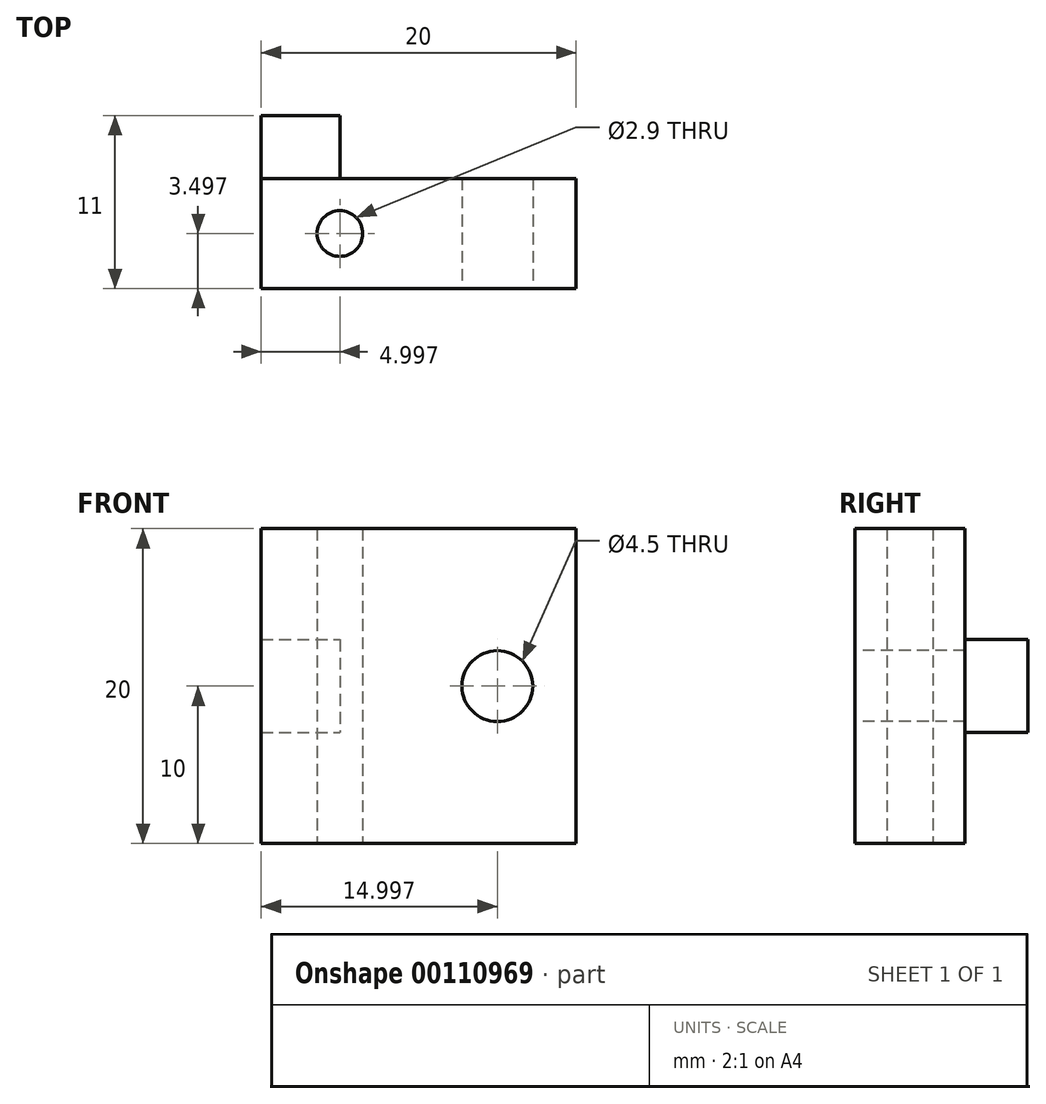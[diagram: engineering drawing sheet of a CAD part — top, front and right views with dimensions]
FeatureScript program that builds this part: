
annotation { "Feature Type Name" : "Feature", "Feature Type Description" : "" }
export const myFeature = defineFeature(function(context is Context, id is Id, definition is map)
    precondition{}
    {
        {
            var Q0;
            Q0=qCreatedBy(makeId("Top.planeOp"),FACE);
            var sketch = newSketch(context, id + "F0", { "sketchPlane" : qUnion([Q0])});
            skLineSegment(sketch, "E0.bottom", {"start": v(-14.26, 17.83) * mm, "end": v(5.74, 17.83) * mm});
            skLineSegment(sketch, "E0.top", {"start": v(-14.26, 24.83) * mm, "end": v(5.74, 24.83) * mm});
            skLineSegment(sketch, "E0.left", {"start": v(-14.26, 17.83) * mm, "end": v(-14.26, 24.83) * mm});
            skLineSegment(sketch, "E0.right", {"start": v(5.74, 17.83) * mm, "end": v(5.74, 24.83) * mm});
            skCircle(sketch, "E1", {"center": v(-9.26, 21.33) * mm, "radius": 1.45 * mm});
            skPoint(sketch, "E2", {"position": v(-14.26, 21.33) * mm});
            skSolve(sketch);
        }
        {
            var Q0;
            Q0=qSketchRegion(id+"F0",true);
            extrude(context, id + "F1", {"entities" : qUnion([Q0]), "depth" : 20 * mm});
        }
        {
            var Q0;
            Q0=makeQuery(id+"F1.opExtrude","SWEPT_FACE",FACE,{"disambiguationData":[OSD([sQuery(id+"F0.wireOp",EDGE,"E0.top")])]});
            var sketch = newSketch(context, id + "F2", { "sketchPlane" : qUnion([Q0])});
            skLineSegment(sketch, "E3.bottom", {"start": v(14.26, 12.95) * mm, "end": v(9.26, 12.95) * mm});
            skLineSegment(sketch, "E3.top", {"start": v(14.26, 7.05) * mm, "end": v(9.26, 7.05) * mm});
            skLineSegment(sketch, "E3.left", {"start": v(14.26, 12.95) * mm, "end": v(14.26, 7.05) * mm});
            skLineSegment(sketch, "E3.right", {"start": v(9.26, 12.95) * mm, "end": v(9.26, 7.05) * mm});
            skLineSegment(sketch, "E4", {"start": v(8.6, 12.95) * mm, "end": v(8.6, 20) * mm});
            skLineSegment(sketch, "E5", {"start": v(8.17, 7.05) * mm, "end": v(8.17, 0) * mm});
            skSolve(sketch);
        }
        {
            var Q0;
            Q0=qSketchRegion(id+"F2",true);
            extrude(context, id + "F3", {"entities" : qUnion([Q0]), "operationType" : NewBodyOperationType.ADD, "depth" : 4 * mm});
        }
        {
            var Q0;
            Q0=makeQuery(id+"F1.opExtrude","SWEPT_FACE",FACE,{"disambiguationData":[OSD([sQuery(id+"F0.wireOp",EDGE,"E0.bottom")])]});
            var sketch = newSketch(context, id + "F4", { "sketchPlane" : qUnion([Q0])});
            skCircle(sketch, "E6", {"center": v(0.74, 10) * mm, "radius": 2.25 * mm});
            skPoint(sketch, "E7", {"position": v(5.74, 10) * mm});
            skSolve(sketch);
        }
        {
            var Q0;
            Q0=qSketchRegion(id+"F4",true);
            extrude(context, id + "F5", {"entities" : qUnion([Q0]), "operationType" : NewBodyOperationType.REMOVE, "oppositeDirection" : true, "depth" : 25 * mm});
        }
    });
